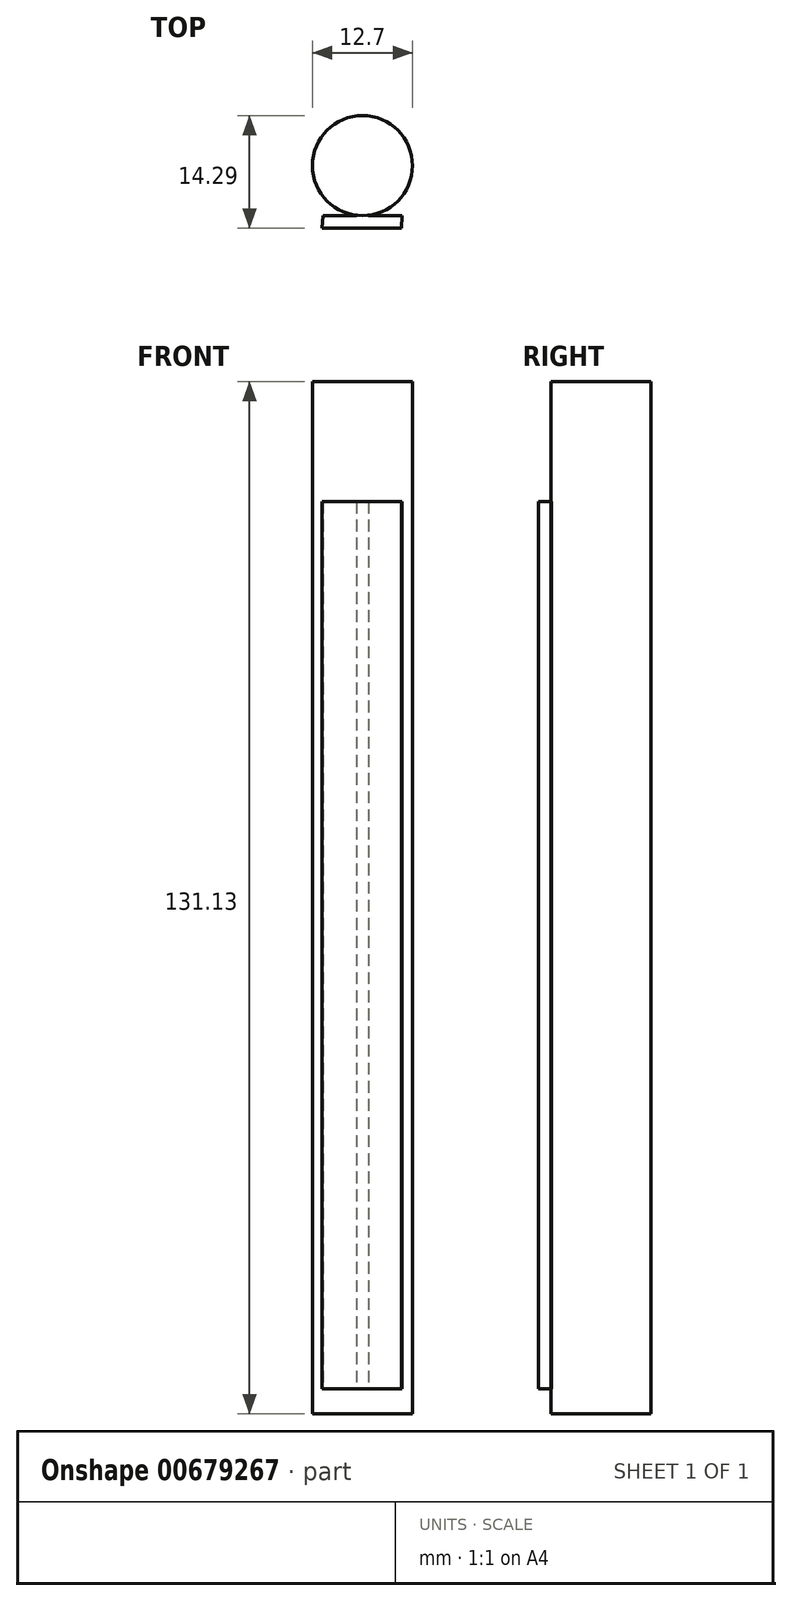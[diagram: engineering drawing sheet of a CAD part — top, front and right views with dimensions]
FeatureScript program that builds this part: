
annotation { "Feature Type Name" : "Feature", "Feature Type Description" : "" }
export const myFeature = defineFeature(function(context is Context, id is Id, definition is map)
    precondition{}
    {
        {
            var Q0;
            Q0=qCreatedBy(makeId("Top.planeOp"),FACE);
            var sketch = newSketch(context, id + "F0", { "sketchPlane" : qUnion([Q0])});
            skArc(sketch, "E0", {"start": v(0.76, -6.3) * mm, "mid": v(0, 6.35) * mm, "end": v(-0.76, -6.3) * mm});
            skLineSegment(sketch, "E1.bottom", {"start": v(4.97, -7.94) * mm, "end": v(-5.11, -7.94) * mm});
            skLineSegment(sketch, "E1.left", {"start": v(4.97, -7.94) * mm, "end": v(5.04, -6.35) * mm});
            skLineSegment(sketch, "E1.right", {"start": v(-5.11, -7.94) * mm, "end": v(-5.04, -6.35) * mm});
            skPoint(sketch, "E1.middle", {"position": v(0, -6.35) * mm});
            skLineSegment(sketch, "E2", {"start": v(-5.04, -6.35) * mm, "end": v(-0.76, -6.35) * mm});
            skPoint(sketch, "E2.endSnap0", {"position": v(5.04, -6.35) * mm});
            skPoint(sketch, "E3.orphan", {"position": v(-4.97, -4.76) * mm});
            skPoint(sketch, "E4.orphan", {"position": v(5.11, -4.76) * mm});
            skPoint(sketch, "E5.orphan", {"position": v(9.86, -6.35) * mm});
            skLineSegment(sketch, "E6", {"start": v(-0.76, -6.3) * mm, "end": v(-0.76, -6.35) * mm});
            skLineSegment(sketch, "E7", {"start": v(0.76, -6.3) * mm, "end": v(0.76, -6.35) * mm});
            skLineSegment(sketch, "E8.trimOffspring", {"start": v(0.76, -6.35) * mm, "end": v(5.04, -6.35) * mm});
            skSolve(sketch);
        }
        {
            var Q0;
            Q0=qSketchRegion(id+"F0",true);
            extrude(context, id + "F1", {"entities" : qUnion([Q0]), "depth" : 112.7 * mm, "offsetDistance" : 25.4 * mm});
        }
        {
            var Q0;
            Q0=makeQuery(id+"F1.opExtrude","CAP_FACE",FACE,{"disambiguationData":[OSD([sQuery(id+"F0.wireOp",EDGE,"E0")])],"isStart":false});
            var sketch = newSketch(context, id + "F2", { "sketchPlane" : qUnion([Q0])});
            skCircle(sketch, "E9", {"center": v(0, 0) * mm, "radius": 6.35 * mm});
            skSolve(sketch);
        }
        {
            var Q0;
            Q0=qSketchRegion(id+"F2",true);
            extrude(context, id + "F3", {"entities" : qUnion([Q0]), "operationType" : NewBodyOperationType.ADD, "depth" : 15.24 * mm, "offsetDistance" : 25.4 * mm});
        }
        {
            var Q0;
            Q0=makeQuery(id+"F1.opExtrude","CAP_FACE",FACE,{"disambiguationData":[OSD([sQuery(id+"F0.wireOp",EDGE,"E0")])],"isStart":true});
            var sketch = newSketch(context, id + "F4", { "sketchPlane" : qUnion([Q0])});
            skCircle(sketch, "E10", {"center": v(0, 0) * mm, "radius": 6.35 * mm});
            skSolve(sketch);
        }
        {
            var Q0;
            Q0=qSketchRegion(id+"F4",true);
            extrude(context, id + "F5", {"entities" : qUnion([Q0]), "operationType" : NewBodyOperationType.ADD, "depth" : 3.17 * mm});
        }
    });
